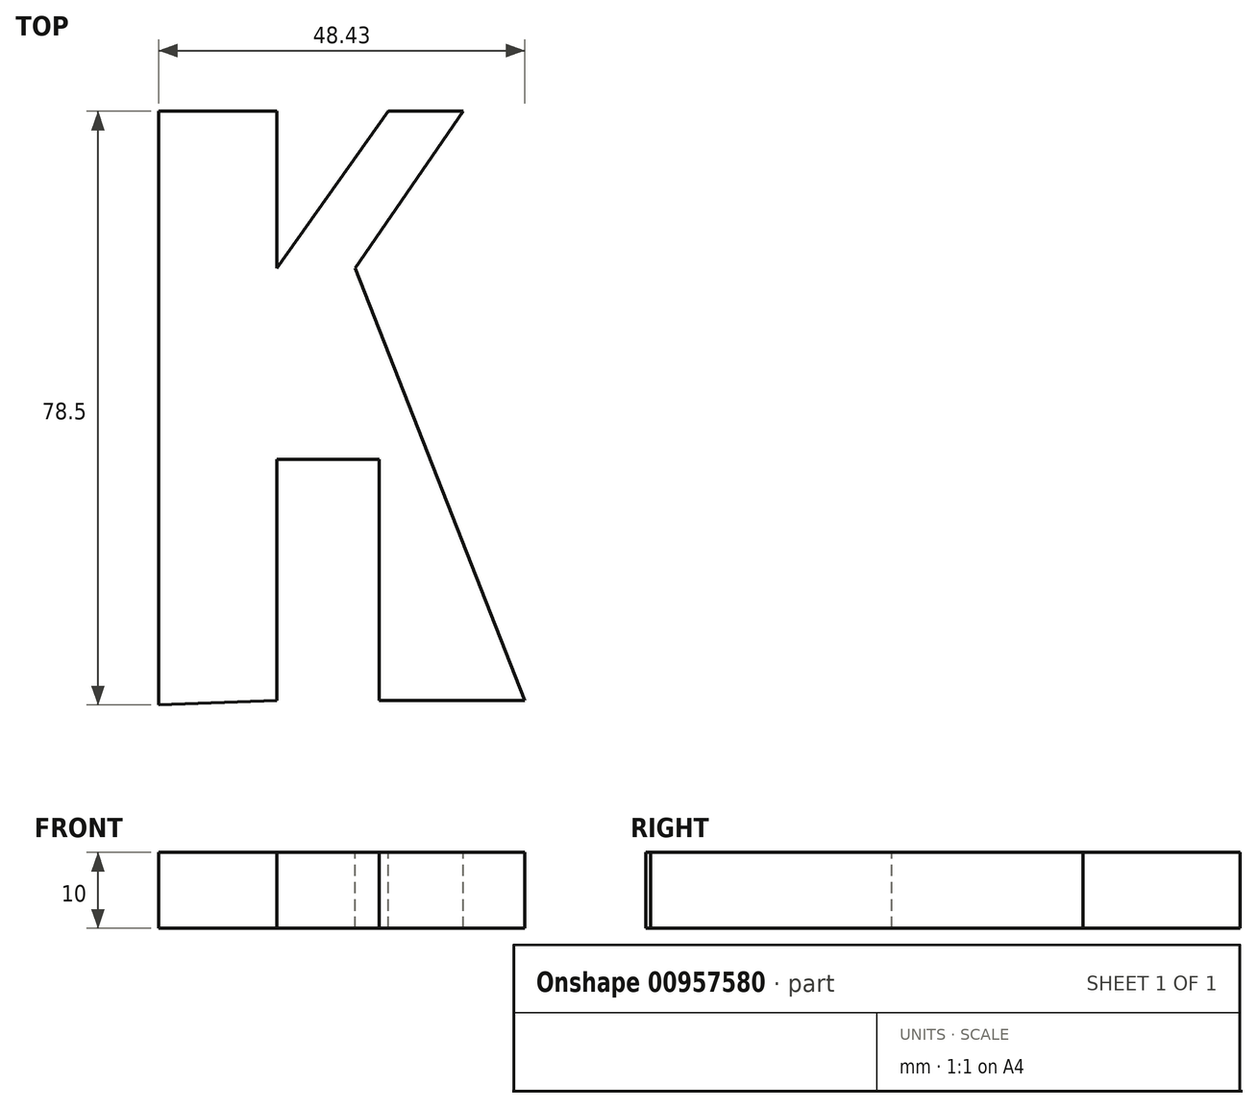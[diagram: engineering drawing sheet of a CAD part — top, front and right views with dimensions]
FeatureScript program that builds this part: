
annotation { "Feature Type Name" : "Feature", "Feature Type Description" : "" }
export const myFeature = defineFeature(function(context is Context, id is Id, definition is map)
    precondition{}
    {
        {
            var Q0;
            Q0=qCreatedBy(makeId("Top.planeOp"),FACE);
            var sketch = newSketch(context, id + "F0", { "sketchPlane" : qUnion([Q0])});
            skLineSegment(sketch, "E0", {"start": v(-26.02, 43.76) * mm, "end": v(-26.02, -34.74) * mm});
            skLineSegment(sketch, "E1", {"start": v(-10.38, 43.76) * mm, "end": v(-10.38, 23.01) * mm});
            skLineSegment(sketch, "E2", {"start": v(-10.38, 23.01) * mm, "end": v(4.36, 43.76) * mm});
            skLineSegment(sketch, "E3", {"start": v(4.36, 43.76) * mm, "end": v(14.29, 43.76) * mm});
            skLineSegment(sketch, "E4", {"start": v(14.29, 43.76) * mm, "end": v(0, 23.01) * mm});
            skLineSegment(sketch, "E5", {"start": v(0, 23.01) * mm, "end": v(22.4, -34.14) * mm});
            skLineSegment(sketch, "E6", {"start": v(22.4, -34.14) * mm, "end": v(3.16, -34.14) * mm});
            skLineSegment(sketch, "E7", {"start": v(3.16, -34.14) * mm, "end": v(3.16, -2.26) * mm});
            skLineSegment(sketch, "E8", {"start": v(3.16, -2.26) * mm, "end": v(-10.38, -2.26) * mm});
            skLineSegment(sketch, "E9", {"start": v(-10.38, -2.26) * mm, "end": v(-10.38, -34.14) * mm});
            skLineSegment(sketch, "E10", {"start": v(-10.38, -34.14) * mm, "end": v(-26.02, -34.74) * mm});
            skLineSegment(sketch, "E11", {"start": v(-26.02, 43.76) * mm, "end": v(-10.38, 43.76) * mm});
            skSolve(sketch);
        }
        {
            var Q0;
            Q0=makeQuery(id+"F0.imprint","IMPRINT",FACE,{"disambiguationData":[TD([[makeQuery(id+"F0.imprint","IMPRINT",EDGE,{"derivedFrom":sQuery(id+"F0.wireOp",EDGE,"E0")}),1.0]])]});
            extrude(context, id + "F1", {"entities" : qUnion([Q0]), "oppositeDirection" : true, "depth" : 10 * mm, "offsetDistance" : 25.4 * mm});
        }
    });
